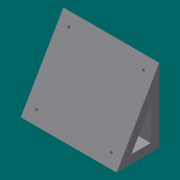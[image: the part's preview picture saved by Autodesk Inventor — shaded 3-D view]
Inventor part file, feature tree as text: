
AUTODESK INVENTOR PART (.ipt)
format: ipt  version: 2013 (Build 170138000, 138)  size: 133,120 bytes
history: native  units: mm
features: sketch x5, extrude x3, hole x2, other x1
ambient origin geometry x8: Origin, YZ Plane, XZ Plane, XY Plane, X Axis, Y Axis, Z Axis, Center Point
feature tree (11):
  other  "ソリッド1"
  extrude  "押し出し1"  Depth=80.0mm
  hole  "穴1"  [1 undecoded]
  hole  "穴2"  [1 undecoded]
  extrude  "押し出し2"  Depth=90.0mm TaperAngle=0.0deg
  extrude  "押し出し3"  Depth=10.0mm
  sketch  "スケッチ1"
  sketch  "スケッチ2"
  sketch  "スケッチ3"
  sketch  "スケッチ4"
  sketch  "スケッチ5"
note: 2 required parameter values undecoded (feature->parameter linkage not recoverable at this tier; creation-order binding heuristic only, values carry confidence <= 0.55)
